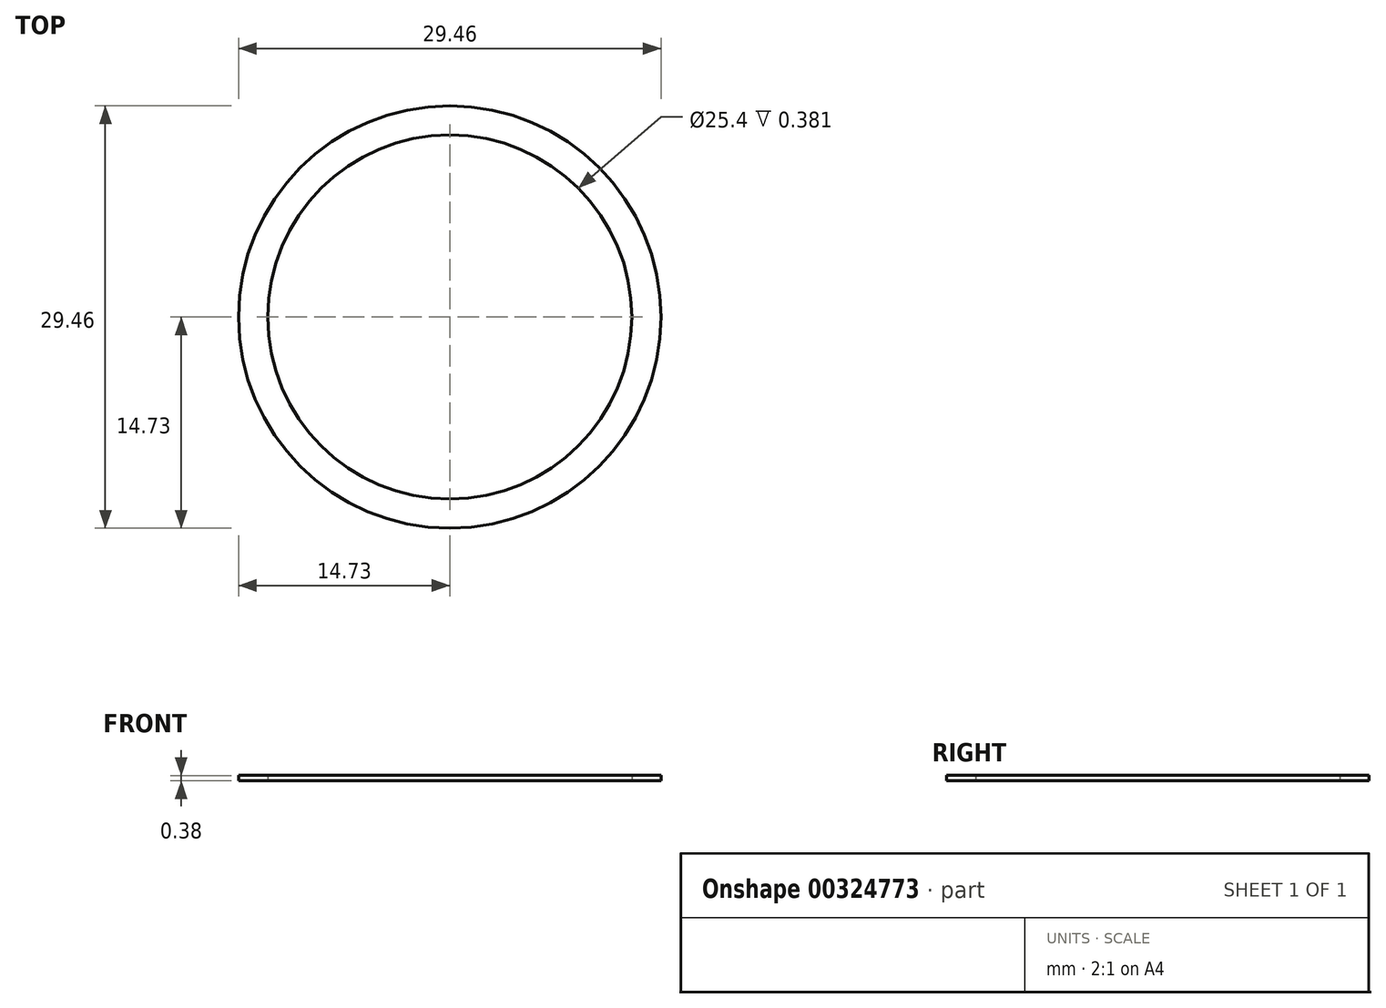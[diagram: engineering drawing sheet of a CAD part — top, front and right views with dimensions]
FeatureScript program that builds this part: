
annotation { "Feature Type Name" : "Feature", "Feature Type Description" : "" }
export const myFeature = defineFeature(function(context is Context, id is Id, definition is map)
    precondition{}
    {
        {
            var Q0;
            Q0=qCreatedBy(makeId("Top.planeOp"),FACE);
            var sketch = newSketch(context, id + "F0", { "sketchPlane" : qUnion([Q0])});
            skCircle(sketch, "E0", {"center": v(0, 0) * mm, "radius": 12.7 * mm});
            skCircle(sketch, "E1", {"center": v(0, 0) * mm, "radius": 14.73 * mm});
            skSolve(sketch);
        }
        {
            var Q0;
            Q0=makeQuery(id+"F0.imprint","IMPRINT",FACE,{"disambiguationData":[TD([[makeQuery(id+"F0.imprint","IMPRINT",EDGE,{"derivedFrom":sQuery(id+"F0.wireOp",EDGE,"E0")}),-1.0]])]});
            extrude(context, id + "F1", {"entities" : qUnion([Q0]), "depth" : 0.38 * mm, "offsetDistance" : 25.4 * mm});
        }
    });
